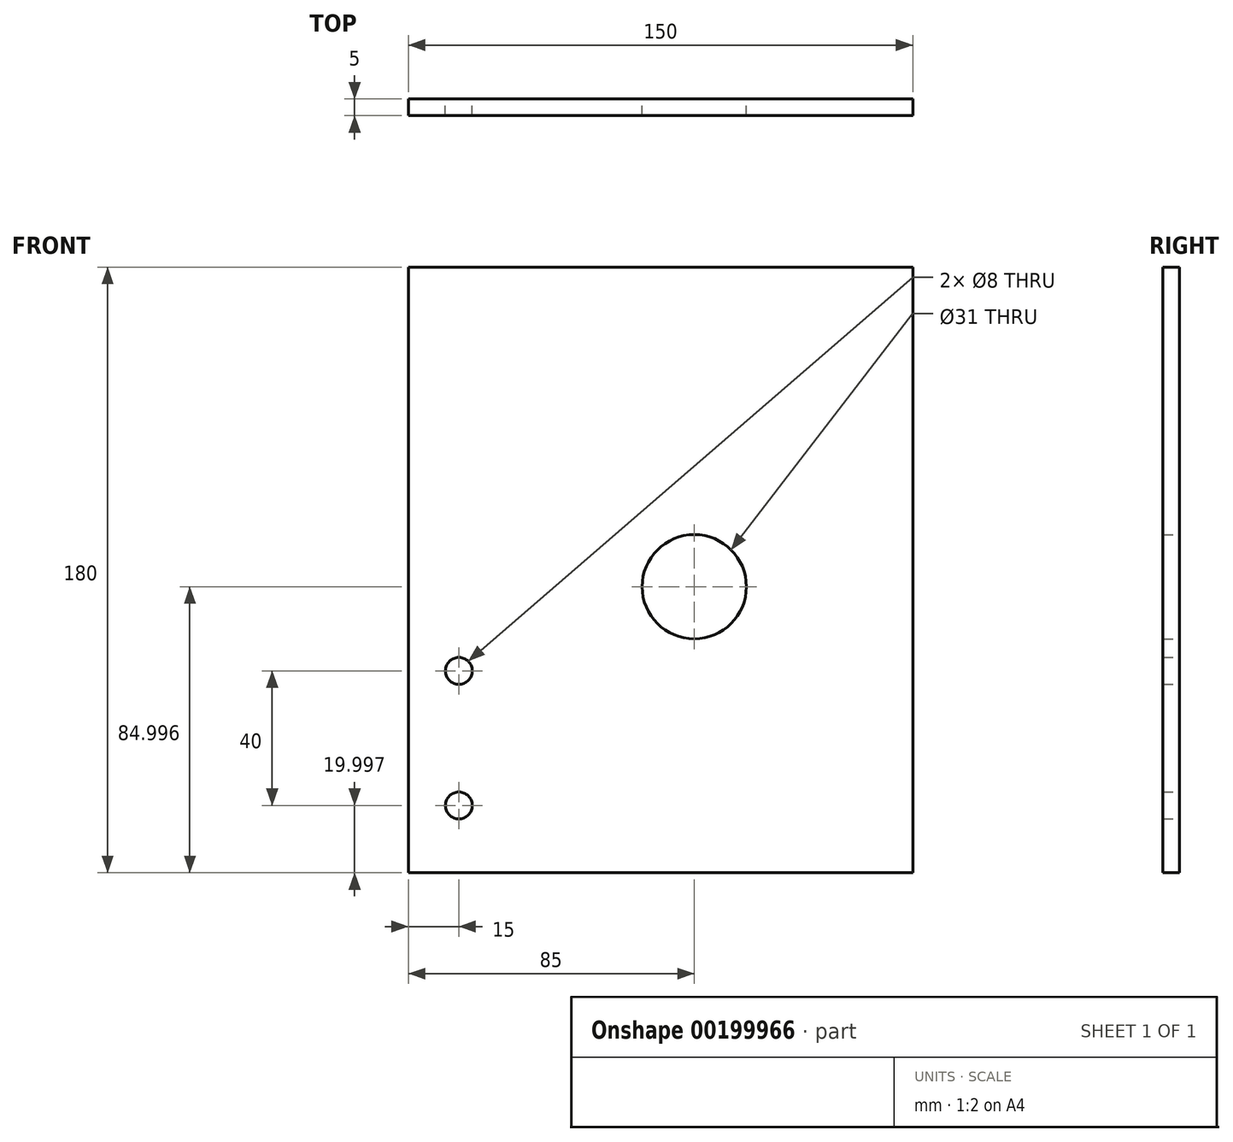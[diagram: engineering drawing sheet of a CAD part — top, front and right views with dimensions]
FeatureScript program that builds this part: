
annotation { "Feature Type Name" : "Feature", "Feature Type Description" : "" }
export const myFeature = defineFeature(function(context is Context, id is Id, definition is map)
    precondition{}
    {
        {
            var Q0;
            Q0=qCreatedBy(makeId("Front.planeOp"),FACE);
            var sketch = newSketch(context, id + "F0", { "sketchPlane" : qUnion([Q0])});
            skLineSegment(sketch, "E0.bottom", {"start": v(65, 108.99) * mm, "end": v(-85, 108.99) * mm});
            skLineSegment(sketch, "E0.top", {"start": v(65, -71.01) * mm, "end": v(-85, -71.01) * mm});
            skLineSegment(sketch, "E0.left", {"start": v(65, 108.99) * mm, "end": v(65, -71.01) * mm});
            skLineSegment(sketch, "E0.right", {"start": v(-85, 108.99) * mm, "end": v(-85, -71.01) * mm});
            skCircle(sketch, "E1", {"center": v(0, 13.99) * mm, "radius": 15.5 * mm});
            skSolve(sketch);
        }
        {
            var Q0;
            Q0 = qSketchRegion(id + "F0", true);
            extrude(context, id + "F1", {"entities" : qUnion([Q0]), "depth" : 5 * mm});
        }
        {
            var Q0;
            Q0=makeQuery(id+"F1.opExtrude","CAP_FACE",FACE,{"disambiguationData":[OSD([sQuery(id+"F0.wireOp",EDGE,"E0.bottom"),sQuery(id+"F0.wireOp",EDGE,"E0.top"),sQuery(id+"F0.wireOp",EDGE,"E0.left"),sQuery(id+"F0.wireOp",EDGE,"E0.right"),sQuery(id+"F0.wireOp",EDGE,"E1")])],"isStart":false});
            var sketch = newSketch(context, id + "F2", { "sketchPlane" : qUnion([Q0])});
            skPoint(sketch, "E2", {"position": v(-70, -51.01) * mm});
            skPoint(sketch, "E3", {"position": v(-70, -11.01) * mm});
            skSolve(sketch);
        }
        {
            var Q0;
            Q0=sQuery(id+"F2.wireOp",VERTEX,"E3");
            var Q1;
            Q1=sQuery(id+"F2.wireOp",VERTEX,"E2");
            var Q2;
            Q2=makeQuery(id+"F1.opExtrude","SWEPT_BODY",BODY,{"disambiguationData":[OSD([sQuery(id+"F0.wireOp",EDGE,"E0.bottom"),sQuery(id+"F0.wireOp",EDGE,"E0.top"),sQuery(id+"F0.wireOp",EDGE,"E0.left"),sQuery(id+"F0.wireOp",EDGE,"E0.right"),sQuery(id+"F0.wireOp",EDGE,"E1")])]});
            hole(context, id + "F3", {"style" : HoleStyle.SIMPLE, "endStyle" : HoleEndStyle.THROUGH, "holeDiameter" : 8 * mm, "locations" : qUnion([Q0, Q1]), "scope" : qUnion([Q2]), "isTappedThrough" : true});
        }
    });
